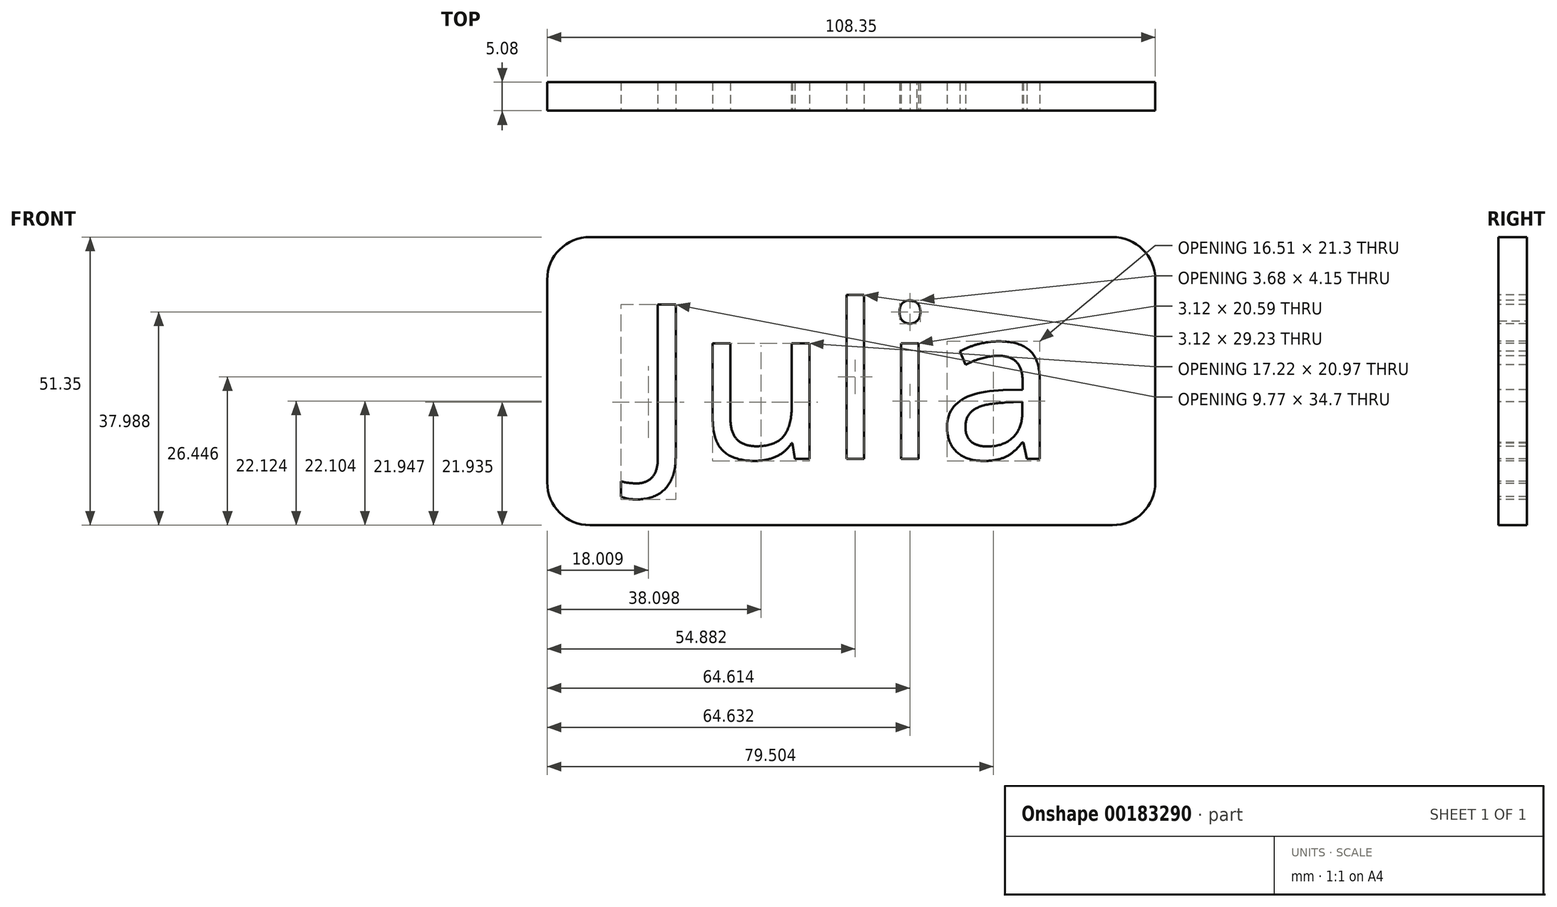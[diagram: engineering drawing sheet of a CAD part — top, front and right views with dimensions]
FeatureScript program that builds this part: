
annotation { "Feature Type Name" : "Feature", "Feature Type Description" : "" }
export const myFeature = defineFeature(function(context is Context, id is Id, definition is map)
    precondition{}
    {
        {
            var Q0;
            Q0=qCreatedBy(makeId("Front.planeOp"),FACE);
            var sketch = newSketch(context, id + "F0", { "sketchPlane" : qUnion([Q0])});
            skLineSegment(sketch, "E0.bottom", {"start": v(-58.6, 27.42) * mm, "end": v(49.74, 27.42) * mm});
            skLineSegment(sketch, "E0.top", {"start": v(-58.6, -23.93) * mm, "end": v(49.74, -23.93) * mm});
            skLineSegment(sketch, "E0.left", {"start": v(-58.6, 27.42) * mm, "end": v(-58.6, -23.93) * mm});
            skLineSegment(sketch, "E0.right", {"start": v(49.74, 27.42) * mm, "end": v(49.74, -23.93) * mm});
            skSolve(sketch);
        }
        {
            var Q0;
            Q0=makeQuery(id+"F0.imprint","IMPRINT",FACE,{"disambiguationData":[TD([[makeQuery(id+"F0.imprint","IMPRINT",EDGE,{"derivedFrom":sQuery(id+"F0.wireOp",EDGE,"E0.bottom")}),-1.0]])]});
            extrude(context, id + "F1", {"entities" : qUnion([Q0]), "depth" : 5.08 * mm});
        }
        {
            var Q0;
            Q0=makeQuery(id+"F1.opExtrude","SWEPT_EDGE",EDGE,{"disambiguationData":[OSD([sQuery(id+"F0.wireOp",EDGE,"E0.bottom"),sQuery(id+"F0.wireOp",EDGE,"E0.left")])]});
            var Q1;
            Q1=makeQuery(id+"F1.opExtrude","SWEPT_EDGE",EDGE,{"disambiguationData":[OSD([sQuery(id+"F0.wireOp",EDGE,"E0.top"),sQuery(id+"F0.wireOp",EDGE,"E0.left")])]});
            var Q2;
            Q2=makeQuery(id+"F1.opExtrude","SWEPT_EDGE",EDGE,{"disambiguationData":[OSD([sQuery(id+"F0.wireOp",EDGE,"E0.bottom"),sQuery(id+"F0.wireOp",EDGE,"E0.right")])]});
            var Q3;
            Q3=makeQuery(id+"F1.opExtrude","SWEPT_EDGE",EDGE,{"disambiguationData":[OSD([sQuery(id+"F0.wireOp",EDGE,"E0.top"),sQuery(id+"F0.wireOp",EDGE,"E0.right")])]});
            fillet(context, id + "F2", {"entities" : qUnion([Q0, Q1, Q2, Q3]), "radius" : 7.62 * mm, "tangentPropagation" : true, "allowEdgeOverflow" : false});
        }
        {
            var Q0;
            Q0=makeQuery(id+"F1.opExtrude","CAP_FACE",FACE,{"disambiguationData":[OSD([sQuery(id+"F0.wireOp",EDGE,"E0.bottom"),sQuery(id+"F0.wireOp",EDGE,"E0.top"),sQuery(id+"F0.wireOp",EDGE,"E0.left"),sQuery(id+"F0.wireOp",EDGE,"E0.right")])],"isStart":false});
            var sketch = newSketch(context, id + "F3", { "sketchPlane" : qUnion([Q0])});
            skText(sketch, "E1", { "text": "Julia", "fontName": "OpenSans-Regular.ttf"});
            const initialGuessF3  = {"E1": [-0.04248, -0.0121, 1, 0, 0.0277]};
            skSetInitialGuess(sketch, initialGuessF3);
            skSolve(sketch);
        }
        {
            var Q0;
            Q0 = qSketchRegion(id + "F3", true);
            extrude(context, id + "F4", {"entities" : qUnion([Q0]), "operationType" : NewBodyOperationType.REMOVE, "endBound" : BoundingType.THROUGH_ALL, "oppositeDirection" : true, "depth" : 1.27 * mm});
        }
    });
